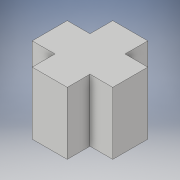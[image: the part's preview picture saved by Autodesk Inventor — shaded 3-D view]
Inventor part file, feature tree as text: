
AUTODESK INVENTOR PART (.ipt)
format: ipt  version: 2019.3 (Build 233278000, 278)  size: 104,960 bytes
history: native  units: mm
features: extrude x1, sketch x1
ambient origin geometry x8: Origin, YZ Plane, XZ Plane, XY Plane, X Axis, Y Axis, Z Axis, Center Point
bodies: Solid1 (feature_tree)
feature tree (2):
  extrude  "Extrusion1"  Depth=10.0mm TaperAngle=0.0deg
  sketch  "Sketch1"  dims[d0=40.0mm d2=360.0deg d4=10.0mm d5=0.0mm]
